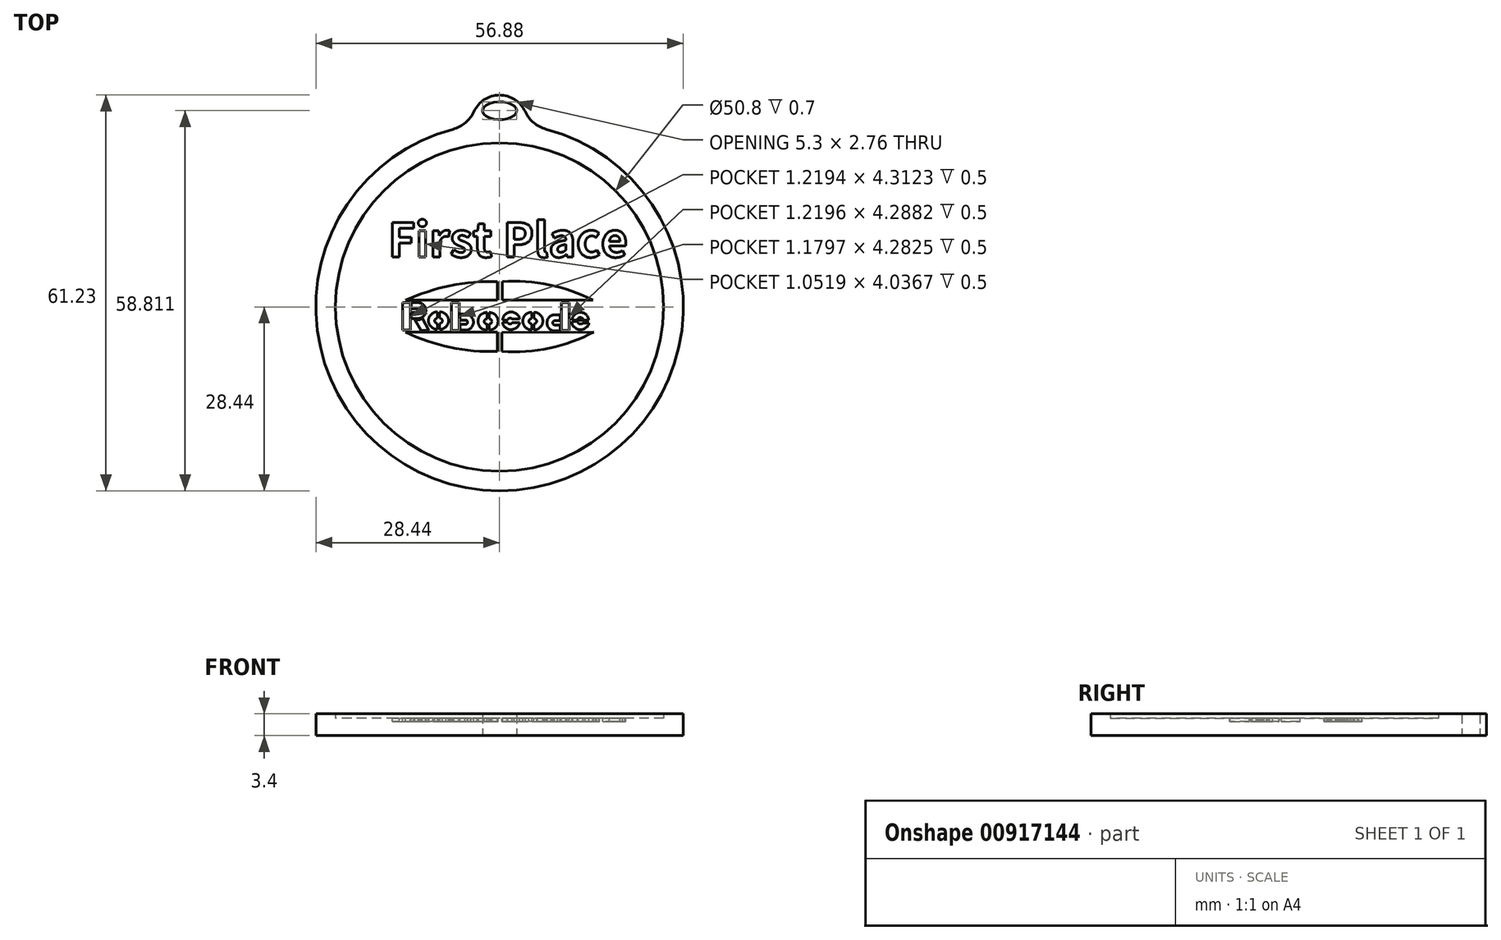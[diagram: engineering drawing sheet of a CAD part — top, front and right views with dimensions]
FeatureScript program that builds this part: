
annotation { "Feature Type Name" : "Feature", "Feature Type Description" : "" }
export const myFeature = defineFeature(function(context is Context, id is Id, definition is map)
    precondition{}
    {
        {
            var Q0;
            Q0=qCreatedBy(makeId("Top.planeOp"),FACE);
            var sketch = newSketch(context, id + "F0", { "sketchPlane" : qUnion([Q0])});
            skCircle(sketch, "E0", {"center": v(0, 0) * mm, "radius": 25.4 * mm});
            skLineSegment(sketch, "E1", {"start": v(0, -25.4) * mm, "end": v(0, 25.4) * mm});
            skArc(sketch, "E2", {"start": v(-7.23, 27.5) * mm, "mid": v(0, -28.44) * mm, "end": v(7.23, 27.5) * mm});
            skArc(sketch, "E3.trimOffspring", {"start": v(3.96, 30.25) * mm, "mid": v(0, 32.79) * mm, "end": v(-3.96, 30.25) * mm});
            skPoint(sketch, "E4.visualSharp", {"position": v(4.34, 28.1) * mm});
            skArc(sketch, "E4.filletArc", {"start": v(3.96, 30.25) * mm, "mid": v(5.28, 28.5) * mm, "end": v(7.23, 27.5) * mm});
            skPoint(sketch, "E5.visualSharp", {"position": v(-4.34, 28.1) * mm});
            skArc(sketch, "E5.filletArc", {"start": v(-7.23, 27.5) * mm, "mid": v(-5.28, 28.5) * mm, "end": v(-3.96, 30.25) * mm});
            skEllipse(sketch, "E6", {"center": v(0, 30.37) * mm, "majorRadius": 2.65 * mm, "minorRadius": 1.38 * mm, "majorAxis": v(1, 0)});
            skSolve(sketch);
        }
        {
            var Q0;
            Q0 = qSketchRegion(id + "F0", true);
            extrude(context, id + "F1", {"entities" : qUnion([Q0]), "depth" : 3.4 * mm, "offsetDistance" : 25 * mm});
        }
        {
            var Q0;
            {var subQ0=sQuery(id+"F0.wireOp",EDGE,"E1");Q0=makeQuery(id+"F0.imprint","IMPRINT",FACE,{"disambiguationData":[TD([[makeQuery(id+"F0.imprint","IMPRINT",EDGE,{"derivedFrom":subQ0}),1.0]])]});}
            var Q1;
            {var subQ0=sQuery(id+"F0.wireOp",EDGE,"E1");Q1=makeQuery(id+"F0.imprint","IMPRINT",FACE,{"disambiguationData":[TD([[makeQuery(id+"F0.imprint","IMPRINT",EDGE,{"derivedFrom":subQ0}),-1.0]])]});}
            extrude(context, id + "F2", {"entities" : qUnion([Q0, Q1]), "operationType" : NewBodyOperationType.ADD, "depth" : 2.7 * mm, "offsetDistance" : 25 * mm});
        }
        {
            var Q0;
            Q0=makeQuery(id+"F2.opExtrude","CAP_FACE",FACE,{"disambiguationData":[OSD([sQuery(id+"F0.wireOp",EDGE,"E0")])],"isStart":false});
            var sketch = newSketch(context, id + "F3", { "sketchPlane" : qUnion([Q0])});
            skLineSegment(sketch, "E7.bottom", {"start": v(-15.01, 0.7) * mm, "end": v(-13.8, 0.7) * mm});
            skLineSegment(sketch, "E7.top", {"start": v(-15.01, -3.6) * mm, "end": v(-13.8, -3.6) * mm});
            skLineSegment(sketch, "E7.left", {"start": v(-15.01, 0.7) * mm, "end": v(-15.01, -3.6) * mm});
            skLineSegment(sketch, "E7.right", {"start": v(-13.8, 0.7) * mm, "end": v(-13.8, -3.6) * mm});
            skLineSegment(sketch, "E8.bottom", {"start": v(-7.45, 0.67) * mm, "end": v(-6.27, 0.67) * mm});
            skLineSegment(sketch, "E8.top", {"start": v(-7.45, -3.61) * mm, "end": v(-6.27, -3.61) * mm});
            skLineSegment(sketch, "E8.left", {"start": v(-7.45, 0.67) * mm, "end": v(-7.45, -3.61) * mm});
            skLineSegment(sketch, "E8.right", {"start": v(-6.27, 0.67) * mm, "end": v(-6.27, -3.61) * mm});
            skLineSegment(sketch, "E9.bottom", {"start": v(9.55, 0.67) * mm, "end": v(10.77, 0.67) * mm});
            skLineSegment(sketch, "E9.top", {"start": v(9.55, -3.62) * mm, "end": v(10.77, -3.62) * mm});
            skLineSegment(sketch, "E9.left", {"start": v(9.55, 0.67) * mm, "end": v(9.55, -3.62) * mm});
            skLineSegment(sketch, "E9.right", {"start": v(10.77, 0.67) * mm, "end": v(10.77, -3.62) * mm});
            skLineSegment(sketch, "E10", {"start": v(-13.67, 0.67) * mm, "end": v(-13.67, -0.27) * mm});
            skLineSegment(sketch, "E11", {"start": v(-13.67, -0.27) * mm, "end": v(-12.73, -0.27) * mm});
            skArc(sketch, "E12", {"start": v(-12.73, -0.85) * mm, "mid": v(-12.44, -0.56) * mm, "end": v(-12.73, -0.27) * mm});
            skLineSegment(sketch, "E13", {"start": v(-12.73, -0.85) * mm, "end": v(-13.67, -0.85) * mm});
            skLineSegment(sketch, "E14", {"start": v(-13.67, -0.85) * mm, "end": v(-13.67, -1.8) * mm});
            skLineSegment(sketch, "E15", {"start": v(-13.67, -1.8) * mm, "end": v(-12.57, -1.8) * mm});
            skLineSegment(sketch, "E16", {"start": v(-13.67, 0.67) * mm, "end": v(-12.57, 0.67) * mm});
            skArc(sketch, "E17", {"start": v(-12.57, -1.8) * mm, "mid": v(-11.4, -0.56) * mm, "end": v(-12.57, 0.67) * mm});
            skArc(sketch, "E18", {"start": v(-13.1, -1.97) * mm, "mid": v(-12.5, -2) * mm, "end": v(-11.97, -1.74) * mm});
            skLineSegment(sketch, "E19", {"start": v(-13.1, -1.97) * mm, "end": v(-12.18, -3.6) * mm});
            skLineSegment(sketch, "E20", {"start": v(-12.18, -3.6) * mm, "end": v(-10.97, -3.6) * mm});
            skLineSegment(sketch, "E21", {"start": v(-10.97, -3.6) * mm, "end": v(-11.97, -1.74) * mm});
            skLineSegment(sketch, "E22", {"start": v(-9.61, -0.76) * mm, "end": v(-9.61, -1.73) * mm});
            skLineSegment(sketch, "E23", {"start": v(-9.61, -2.56) * mm, "end": v(-9.61, -3.48) * mm});
            skArc(sketch, "E24", {"start": v(-9.61, -1.73) * mm, "mid": v(-10.04, -2.14) * mm, "end": v(-9.61, -2.56) * mm});
            skLineSegment(sketch, "E25", {"start": v(-9.29, -0.76) * mm, "end": v(-9.29, -1.73) * mm});
            skLineSegment(sketch, "E26", {"start": v(-9.29, -2.56) * mm, "end": v(-9.29, -3.48) * mm});
            skArc(sketch, "E27", {"start": v(-9.29, -2.56) * mm, "mid": v(-8.86, -2.14) * mm, "end": v(-9.29, -1.73) * mm});
            skArc(sketch, "E28", {"start": v(-9.29, -3.48) * mm, "mid": v(-7.9, -2.12) * mm, "end": v(-9.29, -0.76) * mm});
            skArc(sketch, "E29", {"start": v(-9.61, -0.76) * mm, "mid": v(-11, -2.12) * mm, "end": v(-9.61, -3.48) * mm});
            skLineSegment(sketch, "E30", {"start": v(-1.95, -0.86) * mm, "end": v(-1.95, -1.83) * mm});
            skLineSegment(sketch, "E31", {"start": v(-1.95, -2.65) * mm, "end": v(-1.95, -3.58) * mm});
            skArc(sketch, "E32", {"start": v(-1.95, -1.83) * mm, "mid": v(-2.38, -2.24) * mm, "end": v(-1.95, -2.65) * mm});
            skLineSegment(sketch, "E33", {"start": v(-1.63, -0.86) * mm, "end": v(-1.63, -1.83) * mm});
            skLineSegment(sketch, "E34", {"start": v(-1.63, -2.65) * mm, "end": v(-1.63, -3.58) * mm});
            skArc(sketch, "E35", {"start": v(-1.63, -2.65) * mm, "mid": v(-1.2, -2.24) * mm, "end": v(-1.63, -1.83) * mm});
            skArc(sketch, "E36", {"start": v(-1.63, -3.58) * mm, "mid": v(-0.24, -2.22) * mm, "end": v(-1.63, -0.86) * mm});
            skArc(sketch, "E37", {"start": v(-1.95, -0.86) * mm, "mid": v(-3.34, -2.22) * mm, "end": v(-1.95, -3.58) * mm});
            skLineSegment(sketch, "E38", {"start": v(4.98, -0.83) * mm, "end": v(4.98, -1.8) * mm});
            skLineSegment(sketch, "E39", {"start": v(4.98, -2.62) * mm, "end": v(4.98, -3.55) * mm});
            skArc(sketch, "E40", {"start": v(4.98, -1.8) * mm, "mid": v(4.55, -2.21) * mm, "end": v(4.98, -2.62) * mm});
            skLineSegment(sketch, "E41", {"start": v(5.3, -0.83) * mm, "end": v(5.3, -1.8) * mm});
            skLineSegment(sketch, "E42", {"start": v(5.3, -2.62) * mm, "end": v(5.3, -3.55) * mm});
            skArc(sketch, "E43", {"start": v(5.3, -2.62) * mm, "mid": v(5.73, -2.21) * mm, "end": v(5.3, -1.8) * mm});
            skArc(sketch, "E44", {"start": v(5.3, -3.55) * mm, "mid": v(6.7, -2.19) * mm, "end": v(5.3, -0.83) * mm});
            skArc(sketch, "E45", {"start": v(4.98, -0.83) * mm, "mid": v(3.59, -2.19) * mm, "end": v(4.98, -3.55) * mm});
            skLineSegment(sketch, "E46", {"start": v(-6.1, -1.12) * mm, "end": v(-6.1, -2.02) * mm});
            skLineSegment(sketch, "E47", {"start": v(-6.1, -2.02) * mm, "end": v(-5.3, -2.02) * mm});
            skLineSegment(sketch, "E48", {"start": v(-6.1, -1.12) * mm, "end": v(-5.3, -1.12) * mm});
            skLineSegment(sketch, "E49", {"start": v(-6.1, -2.7) * mm, "end": v(-6.1, -3.6) * mm});
            skLineSegment(sketch, "E50", {"start": v(-6.1, -3.6) * mm, "end": v(-5.3, -3.6) * mm});
            skLineSegment(sketch, "E51", {"start": v(-6.1, -2.7) * mm, "end": v(-5.3, -2.7) * mm});
            skArc(sketch, "E52", {"start": v(-5.3, -2.7) * mm, "mid": v(-4.95, -2.36) * mm, "end": v(-5.3, -2.02) * mm});
            skArc(sketch, "E53", {"start": v(-5.3, -3.6) * mm, "mid": v(-4.05, -2.36) * mm, "end": v(-5.3, -1.12) * mm});
            skLineSegment(sketch, "E54", {"start": v(9.37, -3.7) * mm, "end": v(9.37, -2.8) * mm});
            skLineSegment(sketch, "E55", {"start": v(9.37, -2.8) * mm, "end": v(8.56, -2.8) * mm});
            skLineSegment(sketch, "E56", {"start": v(9.37, -3.7) * mm, "end": v(8.56, -3.7) * mm});
            skLineSegment(sketch, "E57", {"start": v(9.37, -2.12) * mm, "end": v(9.37, -1.22) * mm});
            skLineSegment(sketch, "E58", {"start": v(9.37, -1.22) * mm, "end": v(8.56, -1.22) * mm});
            skLineSegment(sketch, "E59", {"start": v(9.37, -2.12) * mm, "end": v(8.56, -2.12) * mm});
            skArc(sketch, "E60", {"start": v(8.56, -2.12) * mm, "mid": v(8.22, -2.46) * mm, "end": v(8.56, -2.8) * mm});
            skArc(sketch, "E61", {"start": v(8.56, -1.22) * mm, "mid": v(7.32, -2.46) * mm, "end": v(8.56, -3.7) * mm});
            skLineSegment(sketch, "E62", {"start": v(11.21, -2.03) * mm, "end": v(12.03, -2.03) * mm});
            skArc(sketch, "E63", {"start": v(13.8, -2.03) * mm, "mid": v(12.5, -0.83) * mm, "end": v(11.21, -2.03) * mm});
            skArc(sketch, "E64", {"start": v(12.96, -1.97) * mm, "mid": v(12.5, -1.62) * mm, "end": v(12.04, -1.97) * mm});
            skLineSegment(sketch, "E65.trimOffspring", {"start": v(12.97, -2.03) * mm, "end": v(13.8, -2.03) * mm});
            skLineSegment(sketch, "E66", {"start": v(12.03, -2.03) * mm, "end": v(12.97, -2.03) * mm});
            skLineSegment(sketch, "E67", {"start": v(12.04, -1.97) * mm, "end": v(12.96, -1.97) * mm});
            skLineSegment(sketch, "E68", {"start": v(11.21, -2.22) * mm, "end": v(12.03, -2.22) * mm});
            skArc(sketch, "E69", {"start": v(12.03, -2.22) * mm, "mid": v(12.38, -2.62) * mm, "end": v(12.9, -2.49) * mm});
            skLineSegment(sketch, "E70", {"start": v(11.21, -2.22) * mm, "end": v(11.21, -2.62) * mm});
            skArc(sketch, "E71", {"start": v(11.21, -2.62) * mm, "mid": v(12.57, -3.52) * mm, "end": v(13.85, -2.53) * mm});
            skPoint(sketch, "E71.startSnap0", {"position": v(12.38, -2.62) * mm});
            skLineSegment(sketch, "E72", {"start": v(12.9, -2.49) * mm, "end": v(13.85, -2.49) * mm});
            skLineSegment(sketch, "E73", {"start": v(13.85, -2.49) * mm, "end": v(13.85, -2.53) * mm});
            skArc(sketch, "E74", {"start": v(1.94, -1.87) * mm, "mid": v(1.53, -1.71) * mm, "end": v(1.25, -2.06) * mm});
            skArc(sketch, "E75", {"start": v(1.25, -2.36) * mm, "mid": v(1.56, -2.65) * mm, "end": v(1.94, -2.45) * mm});
            skLineSegment(sketch, "E76", {"start": v(1.25, -2.06) * mm, "end": v(0.47, -2.06) * mm});
            skLineSegment(sketch, "E77", {"start": v(1.25, -2.36) * mm, "end": v(0.47, -2.36) * mm});
            skLineSegment(sketch, "E78", {"start": v(1.94, -1.87) * mm, "end": v(3.1, -1.87) * mm});
            skLineSegment(sketch, "E79", {"start": v(1.94, -2.45) * mm, "end": v(3.1, -2.45) * mm});
            skLineSegment(sketch, "E80", {"start": v(0.47, -2.06) * mm, "end": v(0.47, -1.87) * mm});
            skArc(sketch, "E81", {"start": v(3.1, -1.87) * mm, "mid": v(1.8, -0.79) * mm, "end": v(0.47, -1.87) * mm});
            skLineSegment(sketch, "E82", {"start": v(0.47, -2.36) * mm, "end": v(0.47, -2.59) * mm});
            skArc(sketch, "E83", {"start": v(0.47, -2.59) * mm, "mid": v(1.84, -3.5) * mm, "end": v(3.1, -2.45) * mm});
            skLineSegment(sketch, "E84", {"start": v(-0.32, -3.87) * mm, "end": v(-0.32, -6.89) * mm});
            skLineSegment(sketch, "E85", {"start": v(-0.32, -3.87) * mm, "end": v(-14.56, -3.87) * mm});
            skArc(sketch, "E86", {"start": v(-14.56, -3.87) * mm, "mid": v(-7.63, -6.25) * mm, "end": v(-0.32, -6.89) * mm});
            skArc(sketch, "E87", {"start": v(0.38, -6.89) * mm, "mid": v(7.7, -6.38) * mm, "end": v(14.6, -3.88) * mm});
            skLineSegment(sketch, "E88", {"start": v(0.38, -6.89) * mm, "end": v(0.38, -3.92) * mm});
            skLineSegment(sketch, "E89", {"start": v(0.38, -3.92) * mm, "end": v(14.6, -3.88) * mm});
            skArc(sketch, "E90", {"start": v(-0.36, 3.94) * mm, "mid": v(-7.62, 3.3) * mm, "end": v(-14.56, 1.03) * mm});
            skLineSegment(sketch, "E91", {"start": v(-14.56, 1.03) * mm, "end": v(-0.36, 1.03) * mm});
            skLineSegment(sketch, "E92", {"start": v(-0.36, 1.03) * mm, "end": v(-0.36, 3.94) * mm});
            skLineSegment(sketch, "E93", {"start": v(0.43, 3.94) * mm, "end": v(0.43, 1.03) * mm});
            skLineSegment(sketch, "E94", {"start": v(0.43, 1.03) * mm, "end": v(14.46, 1.03) * mm});
            skArc(sketch, "E95", {"start": v(14.46, 1.03) * mm, "mid": v(7.64, 3.44) * mm, "end": v(0.43, 3.94) * mm});
            skSolve(sketch);
        }
        {
            var Q0;
            Q0 = qSketchRegion(id + "F3", true);
            extrude(context, id + "F4", {"entities" : qUnion([Q0]), "operationType" : NewBodyOperationType.REMOVE, "oppositeDirection" : true, "depth" : 0.5 * mm, "offsetDistance" : 25 * mm});
        }
        {
            var Q0;
            {var subQ0=sQuery(id+"F0.wireOp",EDGE,"E0");Q0=makeQuery(id+"F4.boolean.opBoolean","SPLIT",FACE,{"disambiguationData":[TD([makeQuery(id+"F1.opExtrude","SWEPT_FACE",FACE,{"disambiguationData":[OSD([subQ0])]})])],"derivedFrom":makeQuery(id+"F2.opExtrude","CAP_FACE",FACE,{"disambiguationData":[OSD([subQ0])],"isStart":false})});}
            var sketch = newSketch(context, id + "F5", { "sketchPlane" : qUnion([Q0])});
            skText(sketch, "E96", { "text": "First Place ", "fontName": "NotoSansCJKjp-Bold.otf"});
            const initialGuessF5  = {"E96": [-0.01727, 0.00773, 1, 0, 0.00519]};
            skSetInitialGuess(sketch, initialGuessF5);
            skSolve(sketch);
        }
        {
            var Q0;
            Q0 = qSketchRegion(id + "F5", true);
            extrude(context, id + "F6", {"entities" : qUnion([Q0]), "operationType" : NewBodyOperationType.REMOVE, "oppositeDirection" : true, "depth" : 0.5 * mm, "offsetDistance" : 25 * mm});
        }
    });
